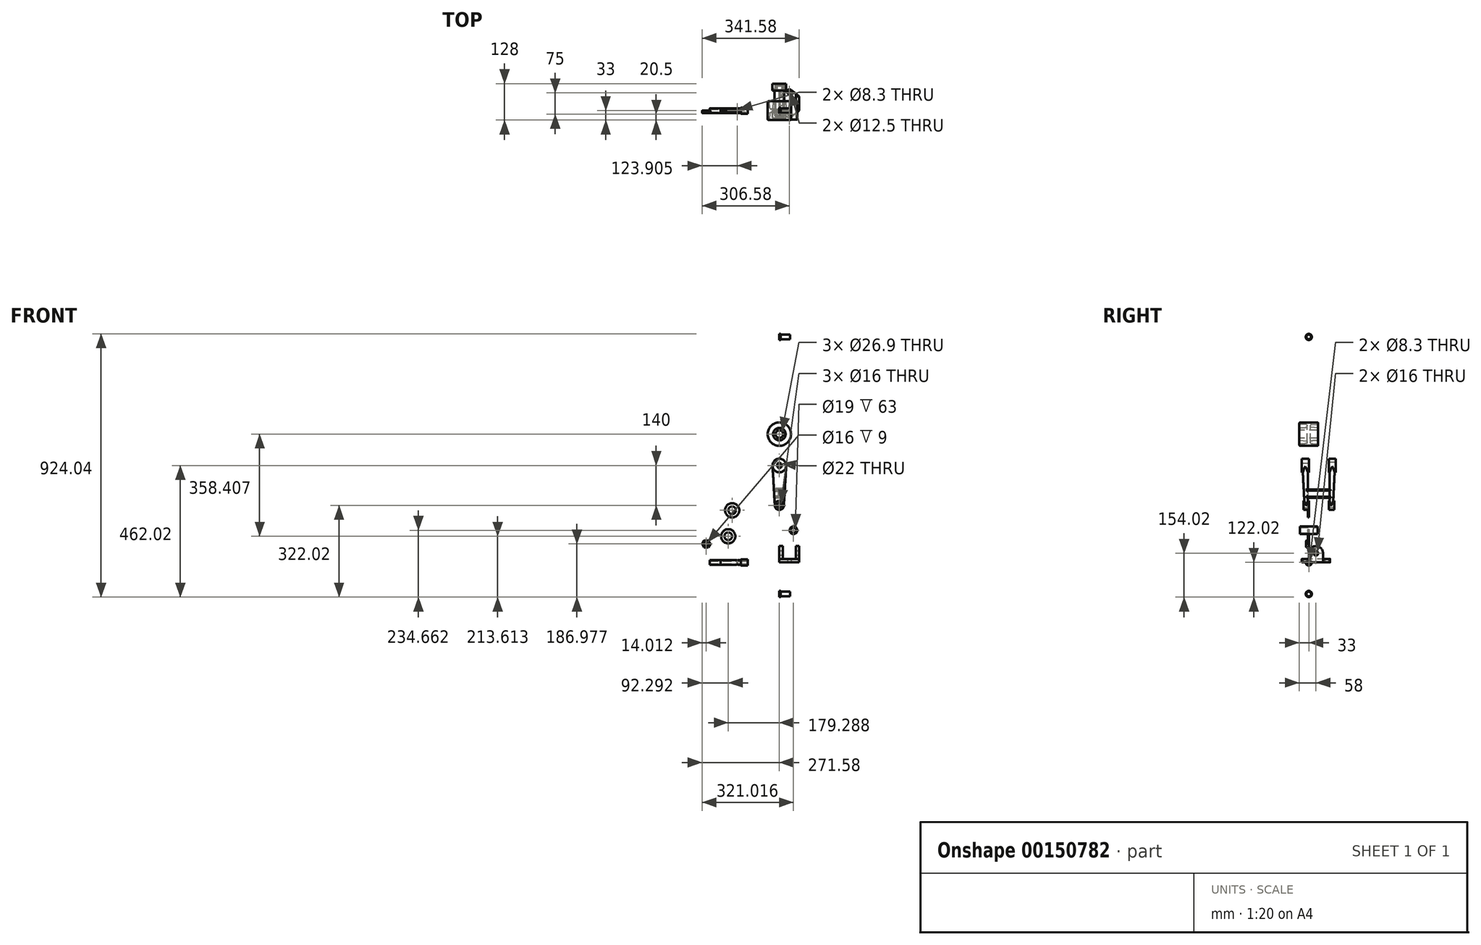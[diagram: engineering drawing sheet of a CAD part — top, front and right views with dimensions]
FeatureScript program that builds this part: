
annotation { "Feature Type Name" : "Feature", "Feature Type Description" : "" }
export const myFeature = defineFeature(function(context is Context, id is Id, definition is map)
    precondition{}
    {
        {
            var Q0;
            Q0=qCreatedBy(makeId("Top.planeOp"),FACE);
            var sketch = newSketch(context, id + "F0", { "sketchPlane" : qUnion([Q0])});
            skLineSegment(sketch, "E0", {"start": v(0, 0) * mm, "end": v(0, 50) * mm});
            skLineSegment(sketch, "E1", {"start": v(0, 50) * mm, "end": v(27.53, 71.9) * mm});
            skLineSegment(sketch, "E2", {"start": v(42.47, 71.9) * mm, "end": v(70, 50) * mm});
            skLineSegment(sketch, "E3", {"start": v(70, 50) * mm, "end": v(70, 0) * mm});
            skLineSegment(sketch, "E4", {"start": v(70, 0) * mm, "end": v(42.47, -21.9) * mm});
            skLineSegment(sketch, "E5", {"start": v(27.53, -21.9) * mm, "end": v(0, 0) * mm});
            skPoint(sketch, "E6.visualSharp", {"position": v(35, 77.83) * mm});
            skArc(sketch, "E6.filletArc", {"start": v(42.47, 71.9) * mm, "mid": v(35, 74.5) * mm, "end": v(27.53, 71.9) * mm});
            skPoint(sketch, "E7.visualSharp", {"position": v(35, -27.83) * mm});
            skArc(sketch, "E7.filletArc", {"start": v(27.53, -21.9) * mm, "mid": v(35, -24.5) * mm, "end": v(42.47, -21.9) * mm});
            skCircle(sketch, "E8", {"center": v(35, -12.5) * mm, "radius": 6.25 * mm});
            skCircle(sketch, "E9", {"center": v(35, 62.5) * mm, "radius": 6.25 * mm});
            skSolve(sketch);
        }
        {
            var Q0;
            Q0=qSketchRegion(id+"F0",true);
            extrude(context, id + "F1", {"entities" : qUnion([Q0]), "depth" : 12 * mm});
        }
        {
            var Q0;
            Q0=qCreatedBy(makeId("Right.planeOp"),FACE);
            var sketch = newSketch(context, id + "F2", { "sketchPlane" : qUnion([Q0])});
            skLineSegment(sketch, "E10", {"start": v(0, 0) * mm, "end": v(0, 32) * mm});
            skLineSegment(sketch, "E11", {"start": v(50, 32) * mm, "end": v(50, 0) * mm});
            skArc(sketch, "E12", {"start": v(50, 32) * mm, "mid": v(25, 57) * mm, "end": v(0, 32) * mm});
            skCircle(sketch, "E13", {"center": v(25, 32) * mm, "radius": 8 * mm});
            skLineSegment(sketch, "E14", {"start": v(0, 0) * mm, "end": v(50, 0) * mm});
            skSolve(sketch);
        }
        {
            var Q0;
            Q0=qSketchRegion(id+"F2",true);
            extrude(context, id + "F3", {"entities" : qUnion([Q0]), "operationType" : NewBodyOperationType.ADD, "depth" : 70 * mm});
        }
        {
            var Q0;
            Q0=qCreatedBy(makeId("Front.planeOp"),FACE);
            var sketch = newSketch(context, id + "F4", { "sketchPlane" : qUnion([Q0])});
            skLineSegment(sketch, "E15", {"start": v(0, 11.9) * mm, "end": v(70, 11.9) * mm, "construction": true});
            skLineSegment(sketch, "E16", {"start": v(12, 11.9) * mm, "end": v(12, 57.9) * mm});
            skLineSegment(sketch, "E17", {"start": v(12, 57.9) * mm, "end": v(58, 57.9) * mm});
            skLineSegment(sketch, "E18", {"start": v(58, 57.9) * mm, "end": v(58, 11.9) * mm});
            skLineSegment(sketch, "E19", {"start": v(12, 11.9) * mm, "end": v(58, 11.9) * mm});
            skSolve(sketch);
        }
        {
            var Q0;
            Q0=qSketchRegion(id+"F4",true);
            extrude(context, id + "F5", {"entities" : qUnion([Q0]), "operationType" : NewBodyOperationType.REMOVE, "endBound" : BoundingType.THROUGH_ALL, "oppositeDirection" : true, "depth" : 25 * mm});
        }
        {
            var Q0;
            Q0=qCreatedBy(makeId("Front.planeOp"),FACE);
            var sketch = newSketch(context, id + "F6", { "sketchPlane" : qUnion([Q0])});
            skCircle(sketch, "E20", {"center": v(0, 200) * mm, "radius": 8 * mm});
            skCircle(sketch, "E21", {"center": v(0, 200) * mm, "radius": 16 * mm});
            skCircle(sketch, "E22", {"center": v(0, 340) * mm, "radius": 11 * mm});
            skCircle(sketch, "E23", {"center": v(0, 340) * mm, "radius": 24 * mm});
            skLineSegment(sketch, "E24", {"start": v(0, 200) * mm, "end": v(0, 200) * mm});
            skLineSegment(sketch, "E25", {"start": v(0, 200) * mm, "end": v(-54.61, 200) * mm, "construction": true});
            skLineSegment(sketch, "E26", {"start": v(0, 340) * mm, "end": v(0, 200) * mm, "construction": true});
            skSolve(sketch);
        }
        {
            var Q0;
            Q0=qCreatedBy(makeId("Right.planeOp"),FACE);
            var sketch = newSketch(context, id + "F7", { "sketchPlane" : qUnion([Q0])});
            skLineSegment(sketch, "E27", {"start": v(0, 0) * mm, "end": v(0, 463.45) * mm, "construction": true});
            skLineSegment(sketch, "E28", {"start": v(0, 463.45) * mm, "end": v(-31.5, 463.45) * mm});
            skLineSegment(sketch, "E29", {"start": v(0, 463.45) * mm, "end": v(31.5, 463.45) * mm});
            skLineSegment(sketch, "E30", {"start": v(-31.5, 463.45) * mm, "end": v(-31.5, 472) * mm});
            skLineSegment(sketch, "E31", {"start": v(31.5, 463.45) * mm, "end": v(31.5, 472) * mm});
            skLineSegment(sketch, "E32", {"start": v(0, 463.45) * mm, "end": v(0, 474) * mm, "construction": true});
            skLineSegment(sketch, "E33", {"start": v(0, 474) * mm, "end": v(-6, 474) * mm, "construction": true});
            skLineSegment(sketch, "E34", {"start": v(0, 474) * mm, "end": v(6, 474) * mm, "construction": true});
            skLineSegment(sketch, "E35", {"start": v(-31.5, 472) * mm, "end": v(-6, 474) * mm});
            skLineSegment(sketch, "E36", {"start": v(6, 474) * mm, "end": v(31.5, 472) * mm});
            skLineSegment(sketch, "E37", {"start": v(0, 450) * mm, "end": v(-20, 450) * mm});
            skLineSegment(sketch, "E38", {"start": v(0, 450) * mm, "end": v(20, 450) * mm});
            skLineSegment(sketch, "E39", {"start": v(6, 474) * mm, "end": v(6, 483) * mm});
            skLineSegment(sketch, "E40", {"start": v(-6, 474) * mm, "end": v(-6, 483) * mm});
            skLineSegment(sketch, "E41", {"start": v(-6, 483) * mm, "end": v(-33, 485) * mm});
            skLineSegment(sketch, "E42", {"start": v(-33, 485) * mm, "end": v(-33, 491) * mm});
            skLineSegment(sketch, "E43", {"start": v(-33, 491) * mm, "end": v(33, 491) * mm});
            skLineSegment(sketch, "E44", {"start": v(33, 491) * mm, "end": v(33, 485) * mm});
            skLineSegment(sketch, "E45", {"start": v(33, 485) * mm, "end": v(6, 483) * mm});
            skSolve(sketch);
        }
        {
            var Q0;
            Q0=qSketchRegion(id+"F7",true);
            var Q1;
            Q1=sQuery(id+"F7.wireOp",EDGE,"E38");
            revolve(context, id + "F8", {"entities" : qUnion([Q0]), "axis" : qUnion([Q1]), "revolveType" : RevolveType.FULL});
        }
        {
            var Q0;
            Q0=makeQuery(id+"F8.opRevolve","SWEPT_EDGE",EDGE,{"disambiguationData":[OSD([sQuery(id+"F7.wireOp",EDGE,"E39"),sQuery(id+"F7.wireOp",EDGE,"E45")])]});
            var Q1;
            Q1=makeQuery(id+"F8.opRevolve","SWEPT_EDGE",EDGE,{"disambiguationData":[OSD([sQuery(id+"F7.wireOp",EDGE,"E36"),sQuery(id+"F7.wireOp",EDGE,"E39")])]});
            var Q2;
            Q2=makeQuery(id+"F8.opRevolve","SWEPT_EDGE",EDGE,{"disambiguationData":[OSD([sQuery(id+"F7.wireOp",EDGE,"E40"),sQuery(id+"F7.wireOp",EDGE,"E41")])]});
            var Q3;
            Q3=makeQuery(id+"F8.opRevolve","SWEPT_EDGE",EDGE,{"disambiguationData":[OSD([sQuery(id+"F7.wireOp",EDGE,"E35"),sQuery(id+"F7.wireOp",EDGE,"E40")])]});
            var Q4;
            Q4=makeQuery(id+"F8.opRevolve","SWEPT_FACE",FACE,{"disambiguationData":[OSD([sQuery(id+"F7.wireOp",EDGE,"E42")])]});
            var Q5;
            Q5=makeQuery(id+"F8.opRevolve","SWEPT_FACE",FACE,{"disambiguationData":[OSD([sQuery(id+"F7.wireOp",EDGE,"E44")])]});
            fillet(context, id + "F9", {"entities" : qUnion([Q0, Q1, Q2, Q3, Q4, Q5]), "radius" : 3 * mm, "tangentPropagation" : true, "allowEdgeOverflow" : false});
        }
        {
            var Q0;
            Q0=qCreatedBy(makeId("Front.planeOp"),FACE);
            var sketch = newSketch(context, id + "F10", { "sketchPlane" : qUnion([Q0])});
            skLineSegment(sketch, "E46", {"start": v(-110.67, 0) * mm, "end": v(-203.02, 0) * mm, "construction": true});
            skLineSegment(sketch, "E47.bottom", {"start": v(-110.67, 4.15) * mm, "end": v(-135.67, 4.15) * mm});
            skLineSegment(sketch, "E47.top", {"start": v(-110.67, 11) * mm, "end": v(-135.67, 11) * mm});
            skLineSegment(sketch, "E47.left", {"start": v(-110.67, 4.15) * mm, "end": v(-110.67, 11) * mm});
            skLineSegment(sketch, "E47.right", {"start": v(-135.67, 4.15) * mm, "end": v(-135.67, 11) * mm});
            skLineSegment(sketch, "E48.bottom", {"start": v(-135.67, 4.15) * mm, "end": v(-205.67, 4.15) * mm});
            skLineSegment(sketch, "E48.top", {"start": v(-135.67, 8.5) * mm, "end": v(-205.67, 8.5) * mm});
            skLineSegment(sketch, "E48.left", {"start": v(-135.67, 4.15) * mm, "end": v(-135.67, 8.5) * mm});
            skLineSegment(sketch, "E48.right", {"start": v(-205.67, 4.15) * mm, "end": v(-205.67, 8.5) * mm});
            skLineSegment(sketch, "E49.bottom", {"start": v(-205.67, 4.15) * mm, "end": v(-244.67, 4.15) * mm});
            skLineSegment(sketch, "E49.top", {"start": v(-205.67, 8) * mm, "end": v(-244.67, 8) * mm});
            skLineSegment(sketch, "E49.left", {"start": v(-205.67, 4.15) * mm, "end": v(-205.67, 8) * mm});
            skLineSegment(sketch, "E49.right", {"start": v(-244.67, 4.15) * mm, "end": v(-244.67, 8) * mm});
            skSolve(sketch);
        }
        {
            var Q0;
            Q0=qSketchRegion(id+"F10",true);
            var Q1;
            Q1=sQuery(id+"F10.wireOp",EDGE,"E46");
            revolve(context, id + "F11", {"entities" : qUnion([Q0]), "axis" : qUnion([Q1]), "revolveType" : RevolveType.FULL});
        }
        {
            var Q0;
            Q0=qCreatedBy(makeId("Top.planeOp"),FACE);
            var sketch = newSketch(context, id + "F12", { "sketchPlane" : qUnion([Q0])});
            skLineSegment(sketch, "E50", {"start": v(-135.67, 0) * mm, "end": v(-147.67, 0) * mm});
            skCircle(sketch, "E51", {"center": v(-147.67, 0) * mm, "radius": 4.15 * mm});
            skSolve(sketch);
        }
        {
            var Q0;
            Q0=sQuery(id+"F6.wireOp",VERTEX,"E23.center");
            var Q1;
            Q1=qCreatedBy(makeId("Top.planeOp"),FACE);
            cPlane(context, id + "F13", {"entities" : qUnion([Q0, Q1]), "cplaneType" : CPlaneType.PLANE_POINT, "offset" : 25 * mm, "width" : 150 * mm, "height" : 150 * mm});
        }
        {
            var Q0;
            Q0=qCreatedBy(makeId("Front.planeOp"),FACE);
            var sketch = newSketch(context, id + "F14", { "sketchPlane" : qUnion([Q0])});
            skLineSegment(sketch, "E52", {"start": v(0, 0) * mm, "end": v(0, 112.64) * mm, "construction": true});
            skLineSegment(sketch, "E53", {"start": v(0, 112.64) * mm, "end": v(49.44, 112.64) * mm, "construction": true});
            skCircle(sketch, "E54", {"center": v(49.44, 112.64) * mm, "radius": 9.5 * mm});
            skCircle(sketch, "E55", {"center": v(49.44, 112.64) * mm, "radius": 13.45 * mm});
            skSolve(sketch);
        }
        {
            var Q0;
            Q0=makeQuery(id+"F6.imprint","IMPRINT",FACE,{"disambiguationData":[TD([[makeQuery(id+"F6.imprint","IMPRINT",EDGE,{"derivedFrom":sQuery(id+"F6.wireOp",EDGE,"E22")}),1.0]])]});
            var Q1;
            Q1=makeQuery(id+"F6.imprint","IMPRINT",FACE,{"disambiguationData":[TD([[makeQuery(id+"F6.imprint","IMPRINT",EDGE,{"derivedFrom":sQuery(id+"F6.wireOp",EDGE,"E22")}),-1.0]])]});
            extrude(context, id + "F15", {"entities" : qUnion([Q0, Q1]), "depth" : 25 * mm});
        }
        {
            var Q0;
            Q0=makeQuery(id+"F6.imprint","IMPRINT",FACE,{"disambiguationData":[TD([[makeQuery(id+"F6.imprint","IMPRINT",EDGE,{"derivedFrom":sQuery(id+"F6.wireOp",EDGE,"E20")}),1.0]])]});
            var Q1;
            Q1=makeQuery(id+"F6.imprint","IMPRINT",FACE,{"disambiguationData":[TD([[makeQuery(id+"F6.imprint","IMPRINT",EDGE,{"derivedFrom":sQuery(id+"F6.wireOp",EDGE,"E20")}),-1.0]])]});
            extrude(context, id + "F16", {"entities" : qUnion([Q0, Q1]), "depth" : 19 * mm});
        }
        {
            var Q0;
            Q0=qSketchRegion(id+"F14",true);
            extrude(context, id + "F17", {"entities" : qUnion([Q0]), "endBound" : BoundingType.SYMMETRIC, "depth" : 63 * mm});
        }
        {
            var Q0;
            Q0=qCreatedBy(id+"F13.planeOp",FACE);
            var sketch = newSketch(context, id + "F18", { "sketchPlane" : qUnion([Q0])});
            skEllipse(sketch, "E56", {"center": v(0, -12.5) * mm, "majorRadius": 24 * mm, "minorRadius": 9.5 * mm, "majorAxis": v(1, 0)});
            skPoint(sketch, "E57", {"position": v(0, -3) * mm});
            skLineSegment(sketch, "E58", {"start": v(24, 0) * mm, "end": v(24, -25) * mm, "construction": true});
            skSolve(sketch);
        }
        {
            var Q0;
            Q0=qSketchRegion(id+"F12",true);
            extrude(context, id + "F19", {"entities" : qUnion([Q0]), "operationType" : NewBodyOperationType.REMOVE, "depth" : 25 * mm, "hasSecondDirection" : true, "secondDirectionOppositeDirection" : true, "secondDirectionDepth" : 25 * mm});
        }
        {
            var Q0;
            Q0=sQuery(id+"F6.wireOp",VERTEX,"E21.center");
            var Q1;
            Q1=qCreatedBy(makeId("Top.planeOp"),FACE);
            cPlane(context, id + "F20", {"entities" : qUnion([Q0, Q1]), "cplaneType" : CPlaneType.PLANE_POINT, "offset" : 25 * mm, "width" : 150 * mm, "height" : 150 * mm});
        }
        {
            var Q0;
            Q0=qCreatedBy(id+"F20.planeOp",FACE);
            var sketch = newSketch(context, id + "F21", { "sketchPlane" : qUnion([Q0])});
            skEllipse(sketch, "E59", {"center": v(0, -9) * mm, "majorRadius": 16 * mm, "minorRadius": 6 * mm, "majorAxis": v(1, 0)});
            skPoint(sketch, "E60", {"position": v(0, -3) * mm});
            skLineSegment(sketch, "E61", {"start": v(16, 0) * mm, "end": v(16, -19) * mm, "construction": true});
            skSolve(sketch);
        }
        {
            var Q0;
            Q0=makeQuery(id+"F18.imprint","IMPRINT",FACE,{"disambiguationData":[TD([[makeQuery(id+"F18.imprint","IMPRINT",EDGE,{"derivedFrom":sQuery(id+"F18.wireOp",EDGE,"E56")}),1.0]])]});
            var Q1;
            Q1=makeQuery(id+"F21.imprint","IMPRINT",FACE,{"disambiguationData":[TD([[makeQuery(id+"F21.imprint","IMPRINT",EDGE,{"derivedFrom":sQuery(id+"F21.wireOp",EDGE,"E59")}),1.0]])]});
            loft(context, id + "F22", {"operationType" : NewBodyOperationType.ADD, "sheetProfilesArray" : [{ "sheetProfileEntities" : qUnion([Q0]) }, { "sheetProfileEntities" : qUnion([Q1]) }]});
        }
        {
            var Q0;
            Q0=makeQuery(id+"F6.imprint","IMPRINT",FACE,{"disambiguationData":[TD([[makeQuery(id+"F6.imprint","IMPRINT",EDGE,{"derivedFrom":sQuery(id+"F6.wireOp",EDGE,"E22")}),1.0]])]});
            var Q1;
            Q1=makeQuery(id+"F6.imprint","IMPRINT",FACE,{"disambiguationData":[TD([[makeQuery(id+"F6.imprint","IMPRINT",EDGE,{"derivedFrom":sQuery(id+"F6.wireOp",EDGE,"E20")}),1.0]])]});
            extrude(context, id + "F23", {"entities" : qUnion([Q0, Q1]), "operationType" : NewBodyOperationType.REMOVE, "endBound" : BoundingType.THROUGH_ALL, "depth" : 25 * mm});
        }
        {
            var Q0;
            Q0=qCreatedBy(makeId("Front.planeOp"),FACE);
            var sketch = newSketch(context, id + "F24", { "sketchPlane" : qUnion([Q0])});
            skCircle(sketch, "E62", {"center": v(-179.29, 91.6) * mm, "radius": 25 * mm});
            skCircle(sketch, "E63", {"center": v(-179.29, 91.6) * mm, "radius": 13.45 * mm});
            skCircle(sketch, "E64", {"center": v(-165.64, 182.83) * mm, "radius": 25 * mm});
            skCircle(sketch, "E65", {"center": v(-165.64, 182.83) * mm, "radius": 13.45 * mm});
            skSolve(sketch);
        }
        {
            var Q0;
            Q0=qSketchRegion(id+"F24",true);
            extrude(context, id + "F25", {"entities" : qUnion([Q0]), "depth" : 3 * mm});
        }
        {
            var Q0;
            Q0=qCreatedBy(makeId("Front.planeOp"),FACE);
            var sketch = newSketch(context, id + "F26", { "sketchPlane" : qUnion([Q0])});
            skLineSegment(sketch, "E66", {"start": v(-264.37, 77.03) * mm, "end": v(-249.51, 77.03) * mm});
            skLineSegment(sketch, "E67", {"start": v(-249.51, 77.03) * mm, "end": v(-242.3, 65.03) * mm});
            skLineSegment(sketch, "E68", {"start": v(-242.3, 65.03) * mm, "end": v(-249.51, 53.03) * mm});
            skLineSegment(sketch, "E69", {"start": v(-249.51, 53.03) * mm, "end": v(-264.37, 53.03) * mm});
            skLineSegment(sketch, "E70", {"start": v(-264.37, 53.03) * mm, "end": v(-271.58, 65.03) * mm});
            skLineSegment(sketch, "E71", {"start": v(-271.58, 65.03) * mm, "end": v(-264.37, 77.03) * mm});
            skCircle(sketch, "E72", {"center": v(-257.57, 64.96) * mm, "radius": 8 * mm});
            skSolve(sketch);
        }
        {
            var Q0;
            Q0=qSketchRegion(id+"F26",true);
            extrude(context, id + "F27", {"entities" : qUnion([Q0]), "depth" : 9 * mm});
        }
        {
            var Q0;
            Q0=makeQuery(id+"F27.opExtrude","CAP_EDGE",EDGE,{"disambiguationData":[OSD([sQuery(id+"F26.wireOp",EDGE,"E66")])],"isStart":false});
            var Q1;
            Q1=makeQuery(id+"F27.opExtrude","CAP_EDGE",EDGE,{"disambiguationData":[OSD([sQuery(id+"F26.wireOp",EDGE,"E71")])],"isStart":false});
            var Q2;
            Q2=makeQuery(id+"F27.opExtrude","CAP_EDGE",EDGE,{"disambiguationData":[OSD([sQuery(id+"F26.wireOp",EDGE,"E70")])],"isStart":false});
            var Q3;
            Q3=makeQuery(id+"F27.opExtrude","CAP_EDGE",EDGE,{"disambiguationData":[OSD([sQuery(id+"F26.wireOp",EDGE,"E69")])],"isStart":false});
            var Q4;
            Q4=makeQuery(id+"F27.opExtrude","CAP_EDGE",EDGE,{"disambiguationData":[OSD([sQuery(id+"F26.wireOp",EDGE,"E68")])],"isStart":false});
            var Q5;
            Q5=makeQuery(id+"F27.opExtrude","CAP_EDGE",EDGE,{"disambiguationData":[OSD([sQuery(id+"F26.wireOp",EDGE,"E67")])],"isStart":false});
            var Q6;
            Q6=makeQuery(id+"F27.opExtrude","CAP_EDGE",EDGE,{"disambiguationData":[OSD([sQuery(id+"F26.wireOp",EDGE,"E67")])],"isStart":true});
            var Q7;
            Q7=makeQuery(id+"F27.opExtrude","CAP_EDGE",EDGE,{"disambiguationData":[OSD([sQuery(id+"F26.wireOp",EDGE,"E70")])],"isStart":true});
            var Q8;
            Q8=makeQuery(id+"F27.opExtrude","CAP_EDGE",EDGE,{"disambiguationData":[OSD([sQuery(id+"F26.wireOp",EDGE,"E71")])],"isStart":true});
            var Q9;
            Q9=makeQuery(id+"F27.opExtrude","CAP_EDGE",EDGE,{"disambiguationData":[OSD([sQuery(id+"F26.wireOp",EDGE,"E66")])],"isStart":true});
            var Q10;
            Q10=makeQuery(id+"F27.opExtrude","CAP_EDGE",EDGE,{"disambiguationData":[OSD([sQuery(id+"F26.wireOp",EDGE,"E69")])],"isStart":true});
            var Q11;
            Q11=makeQuery(id+"F27.opExtrude","CAP_EDGE",EDGE,{"disambiguationData":[OSD([sQuery(id+"F26.wireOp",EDGE,"E68")])],"isStart":true});
            fillet(context, id + "F28", {"entities" : qUnion([Q0, Q1, Q2, Q3, Q4, Q5, Q6, Q7, Q8, Q9, Q10, Q11]), "radius" : 1.5 * mm, "tangentPropagation" : true, "allowEdgeOverflow" : false});
        }
        {
            var Q0;
            Q0=sQuery(id+"F21.wireOp",VERTEX,"E59.center");
            var Q1;
            Q1=qCreatedBy(makeId("Front.planeOp"),FACE);
            cPlane(context, id + "F29", {"entities" : qUnion([Q0, Q1]), "cplaneType" : CPlaneType.PLANE_POINT, "offset" : 25 * mm, "width" : 150 * mm, "height" : 150 * mm});
        }
        {
            var Q0;
            Q0=qCreatedBy(makeId("Right.planeOp"),FACE);
            var sketch = newSketch(context, id + "F30", { "sketchPlane" : qUnion([Q0])});
            skPoint(sketch, "E73.0", {"position": v(0, 200) * mm});
            skPoint(sketch, "E74", {"position": v(35, 200) * mm});
            skSolve(sketch);
        }
        {
            var Q0;
            Q0=sQuery(id+"F30.wireOp",VERTEX,"E74");
            var Q1;
            Q1=qCreatedBy(makeId("Front.planeOp"),FACE);
            cPlane(context, id + "F31", {"entities" : qUnion([Q0, Q1]), "cplaneType" : CPlaneType.PLANE_POINT, "offset" : 25 * mm, "width" : 150 * mm, "height" : 150 * mm});
        }
        {
            var Q0;
            Q0=makeQuery(id+"F15.opExtrude","SWEPT_BODY",BODY,{"disambiguationData":[OSD([sQuery(id+"F6.wireOp",EDGE,"E23")])]});
            var Q1;
            Q1=qCreatedBy(id+"F31.planeOp",FACE);
            mirror(context, id + "F32", {"entities" : qUnion([Q0]), "mirrorPlane" : qUnion([Q1])});
        }
        {
            var Q0;
            Q0=qCreatedBy(id+"F29.planeOp",FACE);
            var sketch = newSketch(context, id + "F33", { "sketchPlane" : qUnion([Q0])});
            skPoint(sketch, "E75.0", {"position": v(0, 200) * mm});
            skLineSegment(sketch, "E76", {"start": v(0, 200) * mm, "end": v(0, 226) * mm, "construction": true});
            skLineSegment(sketch, "E77", {"start": v(0, 226) * mm, "end": v(-17, 226) * mm});
            skLineSegment(sketch, "E78", {"start": v(-17, 226) * mm, "end": v(-17, 230) * mm});
            skLineSegment(sketch, "E79", {"start": v(-17, 230) * mm, "end": v(-2, 230) * mm});
            skLineSegment(sketch, "E80", {"start": v(-2, 230) * mm, "end": v(-2, 252) * mm});
            skLineSegment(sketch, "E81", {"start": v(-2, 252) * mm, "end": v(-17, 252) * mm});
            skLineSegment(sketch, "E82", {"start": v(-17, 252) * mm, "end": v(-17, 256) * mm});
            skLineSegment(sketch, "E83", {"start": v(-17, 256) * mm, "end": v(17, 256) * mm});
            skLineSegment(sketch, "E84", {"start": v(17, 256) * mm, "end": v(17, 252) * mm});
            skLineSegment(sketch, "E85", {"start": v(17, 252) * mm, "end": v(2, 252) * mm});
            skLineSegment(sketch, "E86", {"start": v(2, 252) * mm, "end": v(2, 230) * mm});
            skLineSegment(sketch, "E87", {"start": v(2, 230) * mm, "end": v(17, 230) * mm});
            skLineSegment(sketch, "E88", {"start": v(17, 230) * mm, "end": v(17, 226) * mm});
            skLineSegment(sketch, "E89", {"start": v(0, 226) * mm, "end": v(17, 226) * mm});
            skSolve(sketch);
        }
        {
            var Q0;
            Q0=qSketchRegion(id+"F33",true);
            var Q1;
            Q1=makeQuery(id+"F32.opPattern","COPY",BODY,{"derivedFrom":makeQuery(id+"F15.opExtrude","SWEPT_BODY",BODY,{"disambiguationData":[OSD([sQuery(id+"F6.wireOp",EDGE,"E23")])]}),"instanceName":"1"});
            extrude(context, id + "F34", {"entities" : qUnion([Q0]), "operationType" : NewBodyOperationType.ADD, "endBound" : BoundingType.UP_TO_BODY, "oppositeDirection" : true, "endBoundEntityBody" : qUnion([Q1]), "depth" : 25 * mm});
        }
        {
            var Q0;
            Q0=makeQuery(id+"F34.opExtrude","TWEAK_EDGE",EDGE,{"derivedFrom":[makeQuery(id+"F32.opPattern","COPY",FACE,{"derivedFrom":makeQuery(id+"F22.opLoft","SWEPT_FACE",FACE,{"disambiguationData":[OSD([sQuery(id+"F18.wireOp",EDGE,"E56"),sQuery(id+"F21.wireOp",EDGE,"E59")])]}),"instanceName":"1"}),makeQuery(id+"F33.imprint","IMPRINT",EDGE,{"derivedFrom":sQuery(id+"F33.wireOp",EDGE,"E81")})]});
            var Q1;
            Q1=makeQuery(id+"F34.opExtrude","TWEAK_EDGE",EDGE,{"derivedFrom":[makeQuery(id+"F32.opPattern","COPY",FACE,{"derivedFrom":makeQuery(id+"F22.opLoft","SWEPT_FACE",FACE,{"disambiguationData":[OSD([sQuery(id+"F18.wireOp",EDGE,"E56"),sQuery(id+"F21.wireOp",EDGE,"E59")])]}),"instanceName":"1"}),makeQuery(id+"F33.imprint","IMPRINT",EDGE,{"derivedFrom":sQuery(id+"F33.wireOp",EDGE,"E80")})]});
            var Q2;
            Q2=makeQuery(id+"F34.opExtrude","TWEAK_EDGE",EDGE,{"derivedFrom":[makeQuery(id+"F32.opPattern","COPY",FACE,{"derivedFrom":makeQuery(id+"F22.opLoft","SWEPT_FACE",FACE,{"disambiguationData":[OSD([sQuery(id+"F18.wireOp",EDGE,"E56"),sQuery(id+"F21.wireOp",EDGE,"E59")])]}),"instanceName":"1"}),makeQuery(id+"F33.imprint","IMPRINT",EDGE,{"derivedFrom":sQuery(id+"F33.wireOp",EDGE,"E79")})]});
            var Q3;
            Q3=makeQuery(id+"F34.opExtrude","SWEPT_EDGE",EDGE,{"disambiguationData":[OSD([sQuery(id+"F33.wireOp",EDGE,"E79"),sQuery(id+"F33.wireOp",EDGE,"E80")])]});
            var Q4;
            Q4=makeQuery(id+"F34.boolean.opBoolean","INTERSECT",EDGE,{"derivedFrom":[makeQuery(id+"F22.opLoft","SWEPT_FACE",FACE,{"disambiguationData":[OSD([sQuery(id+"F18.wireOp",EDGE,"E56"),sQuery(id+"F21.wireOp",EDGE,"E59")])]}),makeQuery(id+"F34.opExtrude","SWEPT_FACE",FACE,{"disambiguationData":[OSD([sQuery(id+"F33.wireOp",EDGE,"E79")])]})]});
            var Q5;
            Q5=makeQuery(id+"F34.boolean.opBoolean","INTERSECT",EDGE,{"derivedFrom":[makeQuery(id+"F22.opLoft","SWEPT_FACE",FACE,{"disambiguationData":[OSD([sQuery(id+"F18.wireOp",EDGE,"E56"),sQuery(id+"F21.wireOp",EDGE,"E59")])]}),makeQuery(id+"F34.opExtrude","SWEPT_FACE",FACE,{"disambiguationData":[OSD([sQuery(id+"F33.wireOp",EDGE,"E80")])]})]});
            var Q6;
            Q6=makeQuery(id+"F34.boolean.opBoolean","INTERSECT",EDGE,{"derivedFrom":[makeQuery(id+"F22.opLoft","SWEPT_FACE",FACE,{"disambiguationData":[OSD([sQuery(id+"F18.wireOp",EDGE,"E56"),sQuery(id+"F21.wireOp",EDGE,"E59")])]}),makeQuery(id+"F34.opExtrude","SWEPT_FACE",FACE,{"disambiguationData":[OSD([sQuery(id+"F33.wireOp",EDGE,"E83")])]})]});
            var Q7;
            Q7=makeQuery(id+"F34.boolean.opBoolean","INTERSECT",EDGE,{"derivedFrom":[makeQuery(id+"F22.opLoft","SWEPT_FACE",FACE,{"disambiguationData":[OSD([sQuery(id+"F18.wireOp",EDGE,"E56"),sQuery(id+"F21.wireOp",EDGE,"E59")])]}),makeQuery(id+"F34.opExtrude","SWEPT_FACE",FACE,{"disambiguationData":[OSD([sQuery(id+"F33.wireOp",EDGE,"E81")])]})]});
            var Q8;
            Q8=makeQuery(id+"F34.opExtrude","TWEAK_EDGE",EDGE,{"derivedFrom":[makeQuery(id+"F32.opPattern","COPY",FACE,{"derivedFrom":makeQuery(id+"F22.opLoft","SWEPT_FACE",FACE,{"disambiguationData":[OSD([sQuery(id+"F18.wireOp",EDGE,"E56"),sQuery(id+"F21.wireOp",EDGE,"E59")])]}),"instanceName":"1"}),makeQuery(id+"F33.imprint","IMPRINT",EDGE,{"derivedFrom":sQuery(id+"F33.wireOp",EDGE,"E83")})]});
            var Q9;
            Q9=makeQuery(id+"F34.opExtrude","TWEAK_EDGE",EDGE,{"derivedFrom":[makeQuery(id+"F32.opPattern","COPY",FACE,{"derivedFrom":makeQuery(id+"F22.opLoft","SWEPT_FACE",FACE,{"disambiguationData":[OSD([sQuery(id+"F18.wireOp",EDGE,"E56"),sQuery(id+"F21.wireOp",EDGE,"E59")])]}),"instanceName":"1"}),makeQuery(id+"F33.imprint","IMPRINT",EDGE,{"derivedFrom":sQuery(id+"F33.wireOp",EDGE,"E87")})]});
            var Q10;
            Q10=makeQuery(id+"F34.opExtrude","TWEAK_EDGE",EDGE,{"derivedFrom":[makeQuery(id+"F32.opPattern","COPY",FACE,{"derivedFrom":makeQuery(id+"F22.opLoft","SWEPT_FACE",FACE,{"disambiguationData":[OSD([sQuery(id+"F18.wireOp",EDGE,"E56"),sQuery(id+"F21.wireOp",EDGE,"E59")])]}),"instanceName":"1"}),makeQuery(id+"F33.imprint","IMPRINT",EDGE,{"derivedFrom":sQuery(id+"F33.wireOp",EDGE,"E86")})]});
            var Q11;
            Q11=makeQuery(id+"F34.opExtrude","TWEAK_EDGE",EDGE,{"derivedFrom":[makeQuery(id+"F32.opPattern","COPY",FACE,{"derivedFrom":makeQuery(id+"F22.opLoft","SWEPT_FACE",FACE,{"disambiguationData":[OSD([sQuery(id+"F18.wireOp",EDGE,"E56"),sQuery(id+"F21.wireOp",EDGE,"E59")])]}),"instanceName":"1"}),makeQuery(id+"F33.imprint","IMPRINT",EDGE,{"derivedFrom":sQuery(id+"F33.wireOp",EDGE,"E85")})]});
            var Q12;
            Q12=makeQuery(id+"F34.opExtrude","SWEPT_EDGE",EDGE,{"disambiguationData":[OSD([sQuery(id+"F33.wireOp",EDGE,"E85"),sQuery(id+"F33.wireOp",EDGE,"E86")])]});
            var Q13;
            Q13=makeQuery(id+"F34.opExtrude","SWEPT_EDGE",EDGE,{"disambiguationData":[OSD([sQuery(id+"F33.wireOp",EDGE,"E86"),sQuery(id+"F33.wireOp",EDGE,"E87")])]});
            var Q14;
            Q14=makeQuery(id+"F34.boolean.opBoolean","INTERSECT",EDGE,{"derivedFrom":[makeQuery(id+"F22.opLoft","SWEPT_FACE",FACE,{"disambiguationData":[OSD([sQuery(id+"F18.wireOp",EDGE,"E56"),sQuery(id+"F21.wireOp",EDGE,"E59")])]}),makeQuery(id+"F34.opExtrude","SWEPT_FACE",FACE,{"disambiguationData":[OSD([sQuery(id+"F33.wireOp",EDGE,"E87")])]})]});
            var Q15;
            Q15=makeQuery(id+"F34.boolean.opBoolean","INTERSECT",EDGE,{"derivedFrom":[makeQuery(id+"F22.opLoft","SWEPT_FACE",FACE,{"disambiguationData":[OSD([sQuery(id+"F18.wireOp",EDGE,"E56"),sQuery(id+"F21.wireOp",EDGE,"E59")])]}),makeQuery(id+"F34.opExtrude","SWEPT_FACE",FACE,{"disambiguationData":[OSD([sQuery(id+"F33.wireOp",EDGE,"E86")])]})]});
            var Q16;
            Q16=makeQuery(id+"F34.boolean.opBoolean","INTERSECT",EDGE,{"derivedFrom":[makeQuery(id+"F22.opLoft","SWEPT_FACE",FACE,{"disambiguationData":[OSD([sQuery(id+"F18.wireOp",EDGE,"E56"),sQuery(id+"F21.wireOp",EDGE,"E59")])]}),makeQuery(id+"F34.opExtrude","SWEPT_FACE",FACE,{"disambiguationData":[OSD([sQuery(id+"F33.wireOp",EDGE,"E85")])]})]});
            fillet(context, id + "F35", {"entities" : qUnion([Q0, Q1, Q2, Q3, Q4, Q5, Q6, Q7, Q8, Q9, Q10, Q11, Q12, Q13, Q14, Q15, Q16]), "radius" : 3 * mm, "tangentPropagation" : true, "allowEdgeOverflow" : false});
        }
        {
            var Q0;
            Q0=qCreatedBy(makeId("Front.planeOp"),FACE);
            var sketch = newSketch(context, id + "F36", { "sketchPlane" : qUnion([Q0])});
            skPoint(sketch, "E90.0", {"position": v(0, 340) * mm});
            skCircle(sketch, "E91", {"center": v(0, 340) * mm, "radius": 8 * mm});
            skCircle(sketch, "E92", {"center": v(0, 340) * mm, "radius": 11 * mm});
            skSolve(sketch);
        }
        {
            var Q0;
            Q0=qSketchRegion(id+"F36",true);
            var Q1;
            Q1=makeQuery(id+"F15.opExtrude","CAP_FACE",FACE,{"disambiguationData":[OSD([sQuery(id+"F6.wireOp",EDGE,"E23")])],"isStart":false});
            extrude(context, id + "F37", {"entities" : qUnion([Q0]), "operationType" : NewBodyOperationType.ADD, "endBound" : BoundingType.UP_TO_SURFACE, "endBoundEntityFace" : qUnion([Q1]), "depth" : 25 * mm});
        }
        {
            var Q0;
            Q0=qCreatedBy(makeId("Right.planeOp"),FACE);
            var sketch = newSketch(context, id + "F38", { "sketchPlane" : qUnion([Q0])});
            skCircle(sketch, "E93", {"center": v(0, -111.02) * mm, "radius": 11 * mm});
            skSolve(sketch);
        }
        {
            var Q0;
            Q0=qSketchRegion(id+"F38",true);
            extrude(context, id + "F39", {"entities" : qUnion([Q0]), "depth" : 5 * mm});
        }
        {
            var Q0;
            Q0=makeQuery(id+"F39.opExtrude","CAP_FACE",FACE,{"disambiguationData":[OSD([sQuery(id+"F38.wireOp",EDGE,"E93")])],"isStart":false});
            var sketch = newSketch(context, id + "F40", { "sketchPlane" : qUnion([Q0])});
            skCircle(sketch, "E94", {"center": v(0, -111.02) * mm, "radius": 8 * mm});
            skSolve(sketch);
        }
        {
            var Q0;
            Q0=qSketchRegion(id+"F40",true);
            extrude(context, id + "F41", {"entities" : qUnion([Q0]), "operationType" : NewBodyOperationType.ADD, "depth" : 33 * mm});
        }
        {
            var Q0;
            Q0=makeQuery(id+"F39.opExtrude","SWEPT_BODY",BODY,{"disambiguationData":[OSD([sQuery(id+"F38.wireOp",EDGE,"E93")])]});
            var Q1;
            Q1=qCreatedBy(id+"F13.planeOp",FACE);
            mirror(context, id + "F42", {"entities" : qUnion([Q0]), "mirrorPlane" : qUnion([Q1])});
        }
    });
